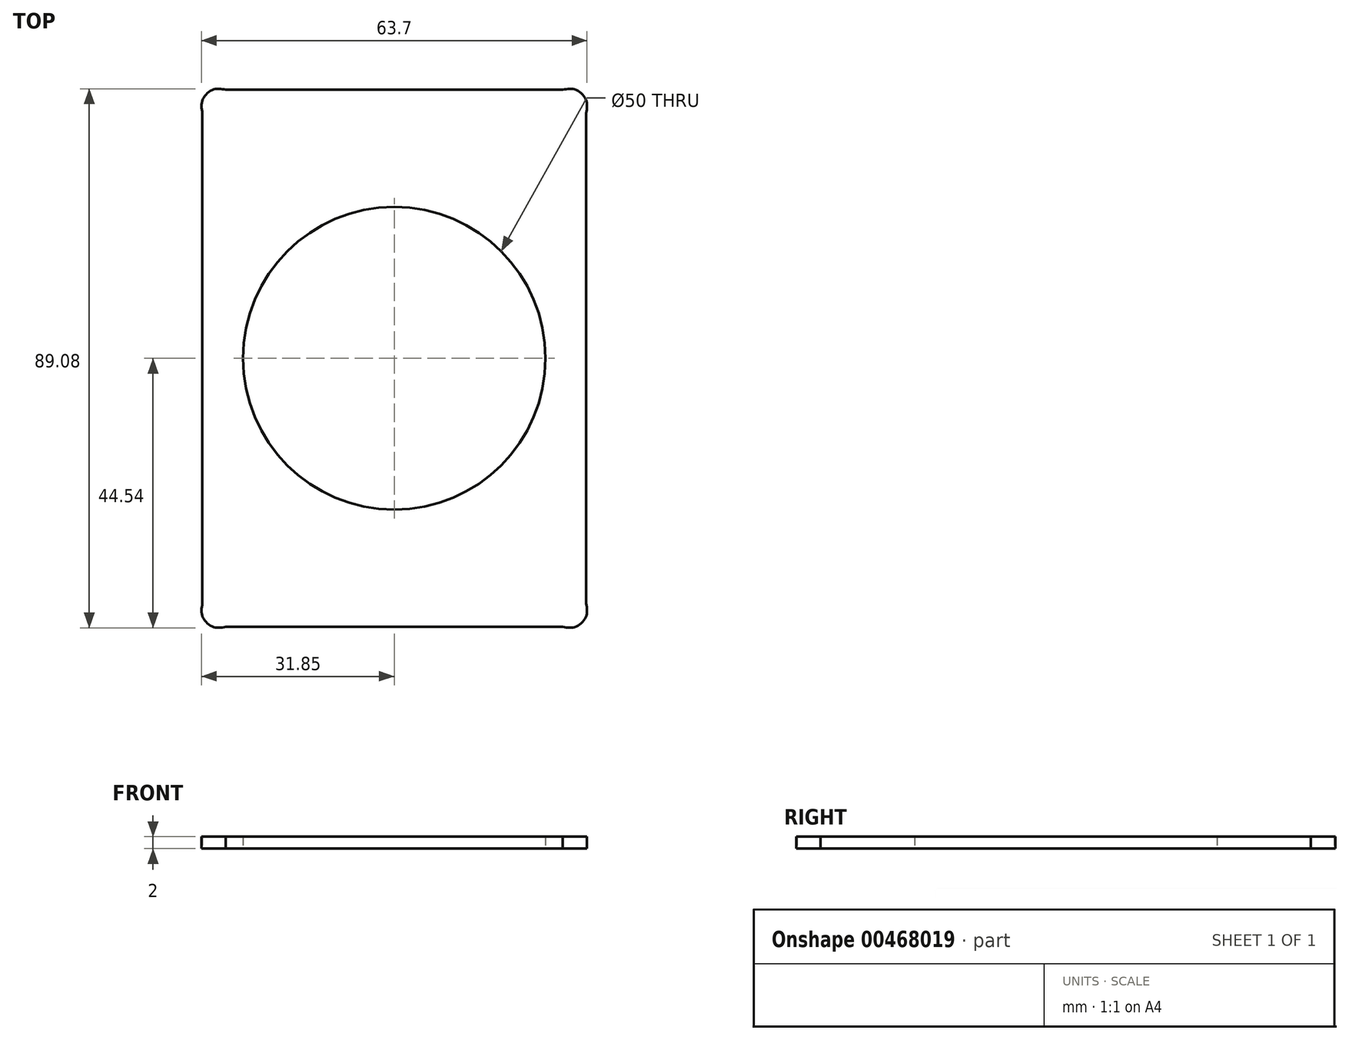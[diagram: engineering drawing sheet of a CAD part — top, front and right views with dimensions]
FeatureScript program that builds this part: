
annotation { "Feature Type Name" : "Feature", "Feature Type Description" : "" }
export const myFeature = defineFeature(function(context is Context, id is Id, definition is map)
    precondition{}
    {
        {
            var Q0;
            Q0=qCreatedBy(makeId("Top.planeOp"),FACE);
            var sketch = newSketch(context, id + "F0", { "sketchPlane" : qUnion([Q0])});
            skLineSegment(sketch, "E0", {"start": v(-31.8, -40.52) * mm, "end": v(-31.8, 40.52) * mm});
            skLineSegment(sketch, "E1", {"start": v(-31.8, 40.52) * mm, "end": v(-31.8, -40.52) * mm});
            skLineSegment(sketch, "E2", {"start": v(-27.84, 44.48) * mm, "end": v(27.84, 44.48) * mm});
            skLineSegment(sketch, "E3", {"start": v(27.84, 44.48) * mm, "end": v(-27.84, 44.48) * mm});
            skLineSegment(sketch, "E4", {"start": v(31.8, 40.52) * mm, "end": v(31.8, -40.52) * mm});
            skLineSegment(sketch, "E5", {"start": v(31.8, -40.52) * mm, "end": v(31.8, 40.52) * mm});
            skLineSegment(sketch, "E6", {"start": v(27.84, -44.48) * mm, "end": v(-27.84, -44.48) * mm});
            skLineSegment(sketch, "E7", {"start": v(-27.84, -44.48) * mm, "end": v(27.84, -44.48) * mm});
            skLineSegment(sketch, "E8", {"start": v(27.84, 44.56) * mm, "end": v(-27.84, 44.56) * mm});
            skLineSegment(sketch, "E9", {"start": v(-31.88, 40.52) * mm, "end": v(-31.88, -40.52) * mm});
            skLineSegment(sketch, "E10", {"start": v(-27.84, -44.56) * mm, "end": v(27.84, -44.56) * mm});
            skLineSegment(sketch, "E11", {"start": v(31.88, -40.52) * mm, "end": v(31.88, 40.52) * mm});
            skLineSegment(sketch, "E12", {"start": v(31.7, 40.52) * mm, "end": v(31.7, -40.52) * mm});
            skLineSegment(sketch, "E13", {"start": v(27.84, -44.39) * mm, "end": v(-27.84, -44.39) * mm});
            skLineSegment(sketch, "E14", {"start": v(-31.7, -40.52) * mm, "end": v(-31.7, 40.52) * mm});
            skLineSegment(sketch, "E15", {"start": v(-27.84, 44.39) * mm, "end": v(27.84, 44.39) * mm});
            skFitSpline(sketch, "E16", {"points": [v(-27.84, -44.48) * mm, v(-30.02, -44.48) * mm, v(-31.8, -42.7) * mm, v(-31.8, -40.52) * mm]});
            skFitSpline(sketch, "E17", {"points": [v(-31.8, 40.52) * mm, v(-31.8, 42.7) * mm, v(-30.02, 44.48) * mm, v(-27.84, 44.48) * mm]});
            skFitSpline(sketch, "E18", {"points": [v(27.84, 44.48) * mm, v(30.02, 44.48) * mm, v(31.8, 42.7) * mm, v(31.8, 40.52) * mm]});
            skFitSpline(sketch, "E19", {"points": [v(31.8, -40.52) * mm, v(31.8, -42.7) * mm, v(30.02, -44.48) * mm, v(27.84, -44.48) * mm]});
            skFitSpline(sketch, "E20", {"points": [v(-27.84, 44.56) * mm, v(-30.07, 44.56) * mm, v(-31.88, 42.75) * mm, v(-31.88, 40.52) * mm]});
            skFitSpline(sketch, "E21", {"points": [v(-31.88, -40.52) * mm, v(-31.88, -42.75) * mm, v(-30.07, -44.56) * mm, v(-27.84, -44.56) * mm]});
            skFitSpline(sketch, "E22", {"points": [v(27.84, -44.56) * mm, v(30.07, -44.56) * mm, v(31.88, -42.75) * mm, v(31.88, -40.52) * mm]});
            skFitSpline(sketch, "E23", {"points": [v(31.88, 40.52) * mm, v(31.88, 42.75) * mm, v(30.07, 44.56) * mm, v(27.84, 44.56) * mm]});
            skFitSpline(sketch, "E24", {"points": [v(27.84, 44.39) * mm, v(29.97, 44.39) * mm, v(31.7, 42.65) * mm, v(31.7, 40.52) * mm]});
            skFitSpline(sketch, "E25", {"points": [v(31.7, -40.52) * mm, v(31.7, -42.65) * mm, v(29.97, -44.39) * mm, v(27.84, -44.39) * mm]});
            skFitSpline(sketch, "E26", {"points": [v(-27.84, -44.39) * mm, v(-29.97, -44.39) * mm, v(-31.7, -42.65) * mm, v(-31.7, -40.52) * mm]});
            skFitSpline(sketch, "E27", {"points": [v(-31.7, 40.52) * mm, v(-31.7, 42.65) * mm, v(-29.97, 44.39) * mm, v(-27.84, 44.39) * mm]});
            skCircle(sketch, "E28", {"center": v(0, 0) * mm, "radius": 25 * mm});
            skSolve(sketch);
        }
        {
            var Q0;
            Q0=makeQuery(id+"F0.imprint","IMPRINT",FACE,{"disambiguationData":[TD([[makeQuery(id+"F0.imprint","IMPRINT",EDGE,{"derivedFrom":sQuery(id+"F0.wireOp",EDGE,"E12")}),-1.0]])]});
            extrude(context, id + "F1", {"entities" : qUnion([Q0]), "depth" : 2 * mm, "offsetDistance" : 25 * mm});
        }
    });
